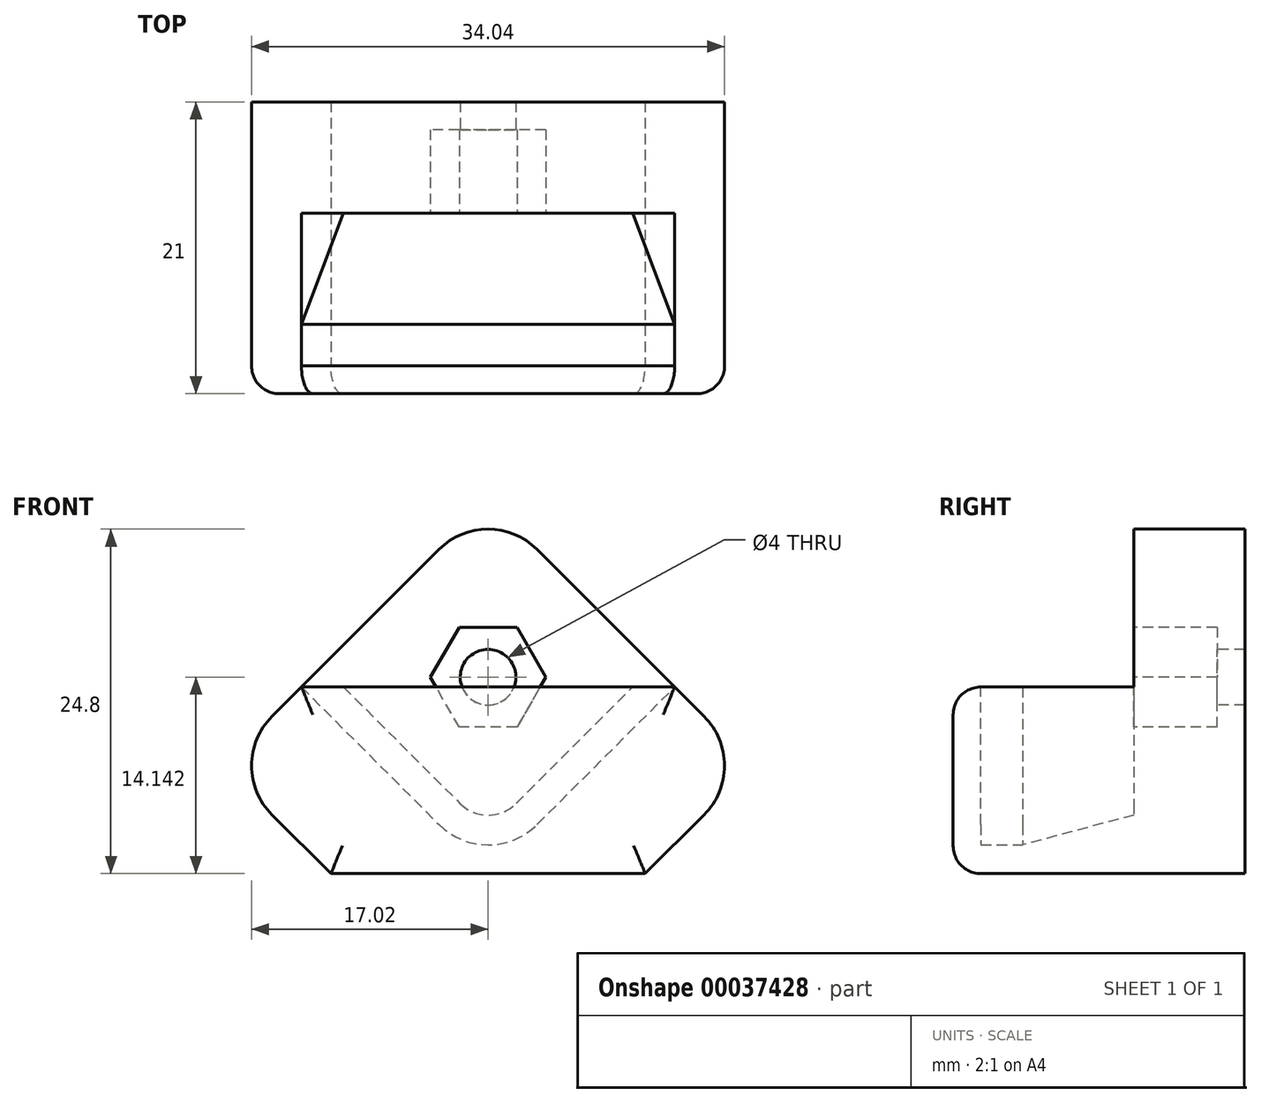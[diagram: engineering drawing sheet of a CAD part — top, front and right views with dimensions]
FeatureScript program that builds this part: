
annotation { "Feature Type Name" : "Feature", "Feature Type Description" : "" }
export const myFeature = defineFeature(function(context is Context, id is Id, definition is map)
    precondition{}
    {
        {
            var Q0;
            Q0=qCreatedBy(makeId("Front.planeOp"),FACE);
            var sketch = newSketch(context, id + "F0", { "sketchPlane" : qUnion([Q0])});
            skLineSegment(sketch, "E0", {"start": v(0, 0) * mm, "end": v(0, 26.87) * mm, "construction": true});
            skLineSegment(sketch, "E1", {"start": v(0, 0) * mm, "end": v(11.31, 0) * mm});
            skLineSegment(sketch, "E2", {"start": v(11.31, 0) * mm, "end": v(19.1, 7.78) * mm});
            skLineSegment(sketch, "E3", {"start": v(19.1, 7.78) * mm, "end": v(0, 26.87) * mm});
            skLineSegment(sketch, "E4", {"start": v(0, 0) * mm, "end": v(13.44, 13.44) * mm});
            skCircle(sketch, "E5", {"center": v(0, 14.14) * mm, "radius": 2 * mm});
            skCircle(sketch, "E6.cCircle", {"center": v(0, 14.14) * mm, "radius": 3.6 * mm, "construction": true});
            skLineSegment(sketch, "E6.0", {"start": v(-2.08, 17.74) * mm, "end": v(2.08, 17.74) * mm});
            skLineSegment(sketch, "E6.1", {"start": v(2.08, 17.74) * mm, "end": v(4.16, 14.14) * mm});
            skLineSegment(sketch, "E6.2", {"start": v(4.16, 14.14) * mm, "end": v(2.08, 10.54) * mm});
            skLineSegment(sketch, "E6.3", {"start": v(2.08, 10.54) * mm, "end": v(-2.08, 10.54) * mm});
            skLineSegment(sketch, "E6.4", {"start": v(-2.08, 10.54) * mm, "end": v(-4.16, 14.14) * mm});
            skLineSegment(sketch, "E6.5", {"start": v(-4.16, 14.14) * mm, "end": v(-2.08, 17.74) * mm});
            skPoint(sketch, "E6.0.midPoint", {"position": v(0, 17.74) * mm});
            skLineSegment(sketch, "E7", {"start": v(0, 13.44) * mm, "end": v(13.44, 13.44) * mm});
            skLineSegment(sketch, "E8.MirrorCS", {"start": v(0, 13.44) * mm, "end": v(-13.44, 13.44) * mm});
            skLineSegment(sketch, "E9.MirrorCS", {"start": v(0, 0) * mm, "end": v(-13.44, 13.44) * mm});
            skLineSegment(sketch, "E10.MirrorCS", {"start": v(-19.1, 7.78) * mm, "end": v(0, 26.87) * mm});
            skLineSegment(sketch, "E11.MirrorCS", {"start": v(-11.31, 0) * mm, "end": v(-19.1, 7.78) * mm});
            skLineSegment(sketch, "E12.MirrorCS", {"start": v(0, 0) * mm, "end": v(-11.31, 0) * mm});
            skLineSegment(sketch, "E13", {"start": v(0, 14.14) * mm, "end": v(6.36, 20.5) * mm, "construction": true});
            skSolve(sketch);
        }
        {
            var Q0;
            {var subQ12=sQuery(id+"F0.wireOp",EDGE,"E6.4");Q0=makeQuery(id+"F0.imprint","IMPRINT",FACE,{"disambiguationData":[TD([[makeQuery(id+"F0.imprint","IMPRINT",EDGE,{"derivedFrom":subQ12}),1.0]])]});}
            var Q1;
            {var subQ8=sQuery(id+"F0.wireOp",EDGE,"E4");Q1=makeQuery(id+"F0.imprint","IMPRINT",FACE,{"disambiguationData":[TD([[makeQuery(id+"F0.imprint","IMPRINT",EDGE,{"derivedFrom":subQ8}),1.0]])]});}
            var Q2;
            {var subQ2=sQuery(id+"F0.wireOp",EDGE,"E9.MirrorCS");Q2=makeQuery(id+"F0.imprint","IMPRINT",FACE,{"disambiguationData":[TD([[makeQuery(id+"F0.imprint","IMPRINT",EDGE,{"derivedFrom":subQ2}),1.0]])]});}
            var Q3;
            Q3=makeQuery(id+"F0.imprint","IMPRINT",FACE,{"disambiguationData":[TD([[makeQuery(id+"F0.imprint","IMPRINT",EDGE,{"derivedFrom":sQuery(id+"F0.wireOp",EDGE,"E1")}),1.0]])]});
            var Q4;
            {var subQ10=sQuery(id+"F0.wireOp",EDGE,"E6.1");Q4=makeQuery(id+"F0.imprint","IMPRINT",FACE,{"disambiguationData":[TD([[makeQuery(id+"F0.imprint","IMPRINT",EDGE,{"derivedFrom":subQ10}),-1.0]])]});}
            var Q5;
            {var subQ6=sQuery(id+"F0.wireOp",EDGE,"E6.4");Q5=makeQuery(id+"F0.imprint","IMPRINT",FACE,{"disambiguationData":[TD([[makeQuery(id+"F0.imprint","IMPRINT",EDGE,{"derivedFrom":subQ6}),-1.0]])]});}
            var Q6;
            Q6=makeQuery(id+"F0.imprint","IMPRINT",FACE,{"disambiguationData":[TD([[makeQuery(id+"F0.imprint","IMPRINT",EDGE,{"derivedFrom":sQuery(id+"F0.wireOp",EDGE,"E6.0")}),1.0]])]});
            extrude(context, id + "F1", {"entities" : qUnion([Q0, Q1, Q2, Q3, Q4, Q5, Q6]), "oppositeDirection" : true, "depth" : 8 * mm});
        }
        {
            var Q0;
            {var subQ10=sQuery(id+"F0.wireOp",EDGE,"E6.1");Q0=makeQuery(id+"F0.imprint","IMPRINT",FACE,{"disambiguationData":[TD([[makeQuery(id+"F0.imprint","IMPRINT",EDGE,{"derivedFrom":subQ10}),-1.0]])]});}
            var Q1;
            {var subQ6=sQuery(id+"F0.wireOp",EDGE,"E6.4");Q1=makeQuery(id+"F0.imprint","IMPRINT",FACE,{"disambiguationData":[TD([[makeQuery(id+"F0.imprint","IMPRINT",EDGE,{"derivedFrom":subQ6}),-1.0]])]});}
            extrude(context, id + "F2", {"entities" : qUnion([Q0, Q1]), "operationType" : NewBodyOperationType.REMOVE, "oppositeDirection" : true, "depth" : 6 * mm});
        }
        {
            var Q0;
            {var subQ2=sQuery(id+"F0.wireOp",EDGE,"E9.MirrorCS");Q0=makeQuery(id+"F0.imprint","IMPRINT",FACE,{"disambiguationData":[TD([[makeQuery(id+"F0.imprint","IMPRINT",EDGE,{"derivedFrom":subQ2}),1.0]])]});}
            var Q1;
            {var subQ8=sQuery(id+"F0.wireOp",EDGE,"E4");Q1=makeQuery(id+"F0.imprint","IMPRINT",FACE,{"disambiguationData":[TD([[makeQuery(id+"F0.imprint","IMPRINT",EDGE,{"derivedFrom":subQ8}),1.0]])]});}
            var Q2;
            Q2=makeQuery(id+"F0.imprint","IMPRINT",FACE,{"disambiguationData":[TD([[makeQuery(id+"F0.imprint","IMPRINT",EDGE,{"derivedFrom":sQuery(id+"F0.wireOp",EDGE,"E1")}),1.0]])]});
            var Q3;
            {var subQ1=sQuery(id+"F0.wireOp",EDGE,"E5");var subQ3=sQuery(id+"F0.wireOp",EDGE,"E7");var subQ5=makeQuery(id+"F0.imprint","INTERSECT",VERTEX,{"derivedFrom":[subQ1,subQ3]});Q3=makeQuery(id+"F0.imprint","IMPRINT",FACE,{"disambiguationData":[TD([[makeQuery(id+"F0.imprint","IMPRINT",EDGE,{"disambiguationData":[TD([[subQ5,1.0]])],"derivedFrom":subQ1}),1.0]])]});}
            var Q4;
            {var subQ8=sQuery(id+"F0.wireOp",EDGE,"E6.3");Q4=makeQuery(id+"F0.imprint","IMPRINT",FACE,{"disambiguationData":[TD([[makeQuery(id+"F0.imprint","IMPRINT",EDGE,{"derivedFrom":subQ8}),-1.0]])]});}
            extrude(context, id + "F3", {"entities" : qUnion([Q0, Q1, Q2, Q3, Q4]), "operationType" : NewBodyOperationType.ADD, "depth" : (10 + 3) * mm});
        }
        {
            var Q0;
            {var subQ12=sQuery(id+"F0.wireOp",EDGE,"E6.4");Q0=makeQuery(id+"F0.imprint","IMPRINT",FACE,{"disambiguationData":[TD([[makeQuery(id+"F0.imprint","IMPRINT",EDGE,{"derivedFrom":subQ12}),1.0]])]});}
            cPlane(context, id + "F4", {"entities" : qUnion([Q0]), "cplaneType" : CPlaneType.OFFSET, "offset" : 8 * mm, "width" : 150 * mm, "height" : 150 * mm});
        }
        {
            var Q0;
            Q0=qCreatedBy(id+"F4.planeOp",FACE);
            var sketch = newSketch(context, id + "F5", { "sketchPlane" : qUnion([Q0])});
            skLineSegment(sketch, "E14.0", {"start": v(-19.1, 7.78) * mm, "end": v(0, 26.87) * mm});
            skLineSegment(sketch, "E15.0", {"start": v(19.1, 7.78) * mm, "end": v(0, 26.87) * mm});
            skLineSegment(sketch, "E16.0", {"start": v(0, 0) * mm, "end": v(13.44, 13.44) * mm});
            skLineSegment(sketch, "E17.0", {"start": v(0, 0) * mm, "end": v(-13.44, 13.44) * mm});
            skArc(sketch, "E18", {"start": v(-3.54, 3.54) * mm, "mid": v(0, 2.07) * mm, "end": v(3.54, 3.54) * mm});
            skSolve(sketch);
        }
        {
            var Q0;
            {var subQ0=sQuery(id+"F5.wireOp",EDGE,"E18");Q0=makeQuery(id+"F5.imprint","IMPRINT",FACE,{"disambiguationData":[TD([[makeQuery(id+"F5.imprint","IMPRINT",EDGE,{"derivedFrom":subQ0}),1.0]])]});}
            extrude(context, id + "F6", {"entities" : qUnion([Q0]), "operationType" : NewBodyOperationType.REMOVE, "oppositeDirection" : true, "depth" : 8 * mm, "hasDraft" : true, "draftAngle" : 15 * degree, "draftPullDirection" : true});
        }
        {
            var Q0;
            {var subQ0=sQuery(id+"F5.wireOp",EDGE,"E18");Q0=makeQuery(id+"F5.imprint","IMPRINT",FACE,{"disambiguationData":[TD([[makeQuery(id+"F5.imprint","IMPRINT",EDGE,{"derivedFrom":subQ0}),1.0]])]});}
            extrude(context, id + "F7", {"entities" : qUnion([Q0]), "operationType" : NewBodyOperationType.REMOVE, "depth" : 3 * mm});
        }
        {
            var Q0;
            {var subQ0=sQuery(id+"F0.wireOp",EDGE,"E10.MirrorCS");var subQ1=sQuery(id+"F0.wireOp",EDGE,"E11.MirrorCS");Q0=makeQuery(id+"F3.boolean.opBoolean","MERGE",EDGE,{"derivedFrom":[makeQuery(id+"F1.opExtrude","SWEPT_EDGE",EDGE,{"disambiguationData":[OSD([subQ0,subQ1])]}),makeQuery(id+"F3.opExtrude","SWEPT_EDGE",EDGE,{"disambiguationData":[OSD([subQ0,subQ1])]})]});}
            var Q1;
            Q1=makeQuery(id+"F1.opExtrude","SWEPT_EDGE",EDGE,{"disambiguationData":[OSD([sQuery(id+"F0.wireOp",EDGE,"E3"),sQuery(id+"F0.wireOp",EDGE,"E10.MirrorCS")])]});
            var Q2;
            {var subQ0=sQuery(id+"F0.wireOp",EDGE,"E2");var subQ1=sQuery(id+"F0.wireOp",EDGE,"E3");Q2=makeQuery(id+"F3.boolean.opBoolean","MERGE",EDGE,{"derivedFrom":[makeQuery(id+"F1.opExtrude","SWEPT_EDGE",EDGE,{"disambiguationData":[OSD([subQ0,subQ1])]}),makeQuery(id+"F3.opExtrude","SWEPT_EDGE",EDGE,{"disambiguationData":[OSD([subQ0,subQ1])]})]});}
            fillet(context, id + "F8", {"entities" : qUnion([Q0, Q1, Q2]), "radius" : 5 * mm, "tangentPropagation" : true, "allowEdgeOverflow" : false});
        }
        {
            var Q0;
            Q0=makeQuery(id+"F3.opExtrude","CAP_FACE",FACE,{"disambiguationData":[OSD([sQuery(id+"F0.wireOp",EDGE,"E1"),sQuery(id+"F0.wireOp",EDGE,"E2"),sQuery(id+"F0.wireOp",EDGE,"E3"),sQuery(id+"F0.wireOp",EDGE,"E7"),sQuery(id+"F0.wireOp",EDGE,"E8.MirrorCS"),sQuery(id+"F0.wireOp",EDGE,"E10.MirrorCS"),sQuery(id+"F0.wireOp",EDGE,"E11.MirrorCS"),sQuery(id+"F0.wireOp",EDGE,"E12.MirrorCS")])],"isStart":false});
            fillet(context, id + "F9", {"entities" : qUnion([Q0]), "radius" : 2 * mm, "tangentPropagation" : true, "allowEdgeOverflow" : false});
        }
    });
